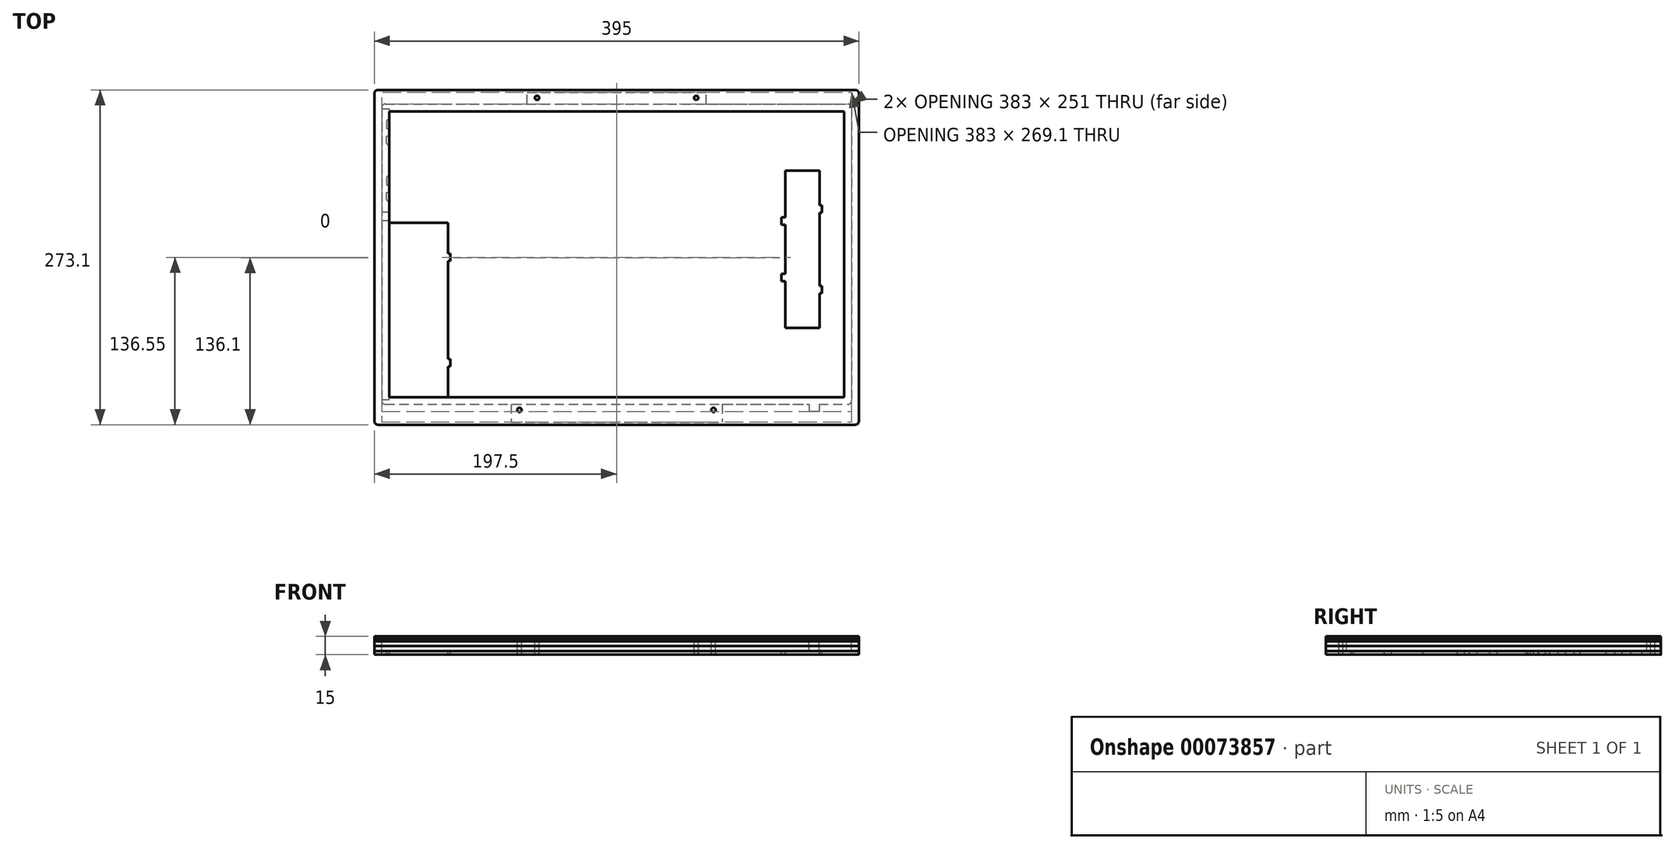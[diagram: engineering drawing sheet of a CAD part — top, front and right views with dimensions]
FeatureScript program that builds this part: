
annotation { "Feature Type Name" : "Feature", "Feature Type Description" : "" }
export const myFeature = defineFeature(function(context is Context, id is Id, definition is map)
    precondition{}
    {
        {
            var Q0;
            Q0=qCreatedBy(makeId("Top.planeOp"),FACE);
            var sketch = newSketch(context, id + "F0", { "sketchPlane" : qUnion([Q0])});
            skLineSegment(sketch, "E0.bottom", {"start": v(3, 245) * mm, "end": v(380, 245) * mm});
            skLineSegment(sketch, "E0.top", {"start": v(3, 0) * mm, "end": v(107.5, 0) * mm});
            skLineSegment(sketch, "E0.left", {"start": v(0, 242) * mm, "end": v(0, 3) * mm});
            skLineSegment(sketch, "E0.right", {"start": v(383, 242) * mm, "end": v(383, 3) * mm});
            skLineSegment(sketch, "E1.bottom", {"start": v(7, 239) * mm, "end": v(376, 239) * mm});
            skLineSegment(sketch, "E1.top", {"start": v(7, 6) * mm, "end": v(376, 6) * mm});
            skLineSegment(sketch, "E1.left", {"start": v(6, 238) * mm, "end": v(6, 7) * mm});
            skLineSegment(sketch, "E1.right", {"start": v(377, 238) * mm, "end": v(377, 7) * mm});
            skLineSegment(sketch, "E2.bottom", {"start": v(124, 253.5) * mm, "end": v(139, 253.5) * mm});
            skLineSegment(sketch, "E2.top", {"start": v(120.5, 245) * mm, "end": v(142.5, 245) * mm});
            skLineSegment(sketch, "E2.left", {"start": v(120.5, 250) * mm, "end": v(120.5, 245) * mm});
            skLineSegment(sketch, "E2.right", {"start": v(142.5, 250) * mm, "end": v(142.5, 245) * mm});
            skPoint(sketch, "E3.visualSharp", {"position": v(6, 239) * mm});
            skArc(sketch, "E3.filletArc", {"start": v(7, 239) * mm, "mid": v(6.3, 238.7) * mm, "end": v(6, 238) * mm});
            skPoint(sketch, "E4.visualSharp", {"position": v(377, 239) * mm});
            skArc(sketch, "E4.filletArc", {"start": v(377, 238) * mm, "mid": v(376.7, 238.7) * mm, "end": v(376, 239) * mm});
            skPoint(sketch, "E5.visualSharp", {"position": v(377, 6) * mm});
            skArc(sketch, "E5.filletArc", {"start": v(376, 6) * mm, "mid": v(376.7, 6.3) * mm, "end": v(377, 7) * mm});
            skPoint(sketch, "E6.visualSharp", {"position": v(6, 6) * mm});
            skArc(sketch, "E6.filletArc", {"start": v(6, 7) * mm, "mid": v(6.3, 6.3) * mm, "end": v(7, 6) * mm});
            skPoint(sketch, "E7.visualSharp", {"position": v(0, 245) * mm});
            skArc(sketch, "E7.filletArc", {"start": v(3, 245) * mm, "mid": v(0.88, 244.12) * mm, "end": v(0, 242) * mm});
            skPoint(sketch, "E8.visualSharp", {"position": v(383, 245) * mm});
            skArc(sketch, "E8.filletArc", {"start": v(383, 242) * mm, "mid": v(382.12, 244.12) * mm, "end": v(380, 245) * mm});
            skPoint(sketch, "E9.visualSharp", {"position": v(383, 0) * mm});
            skArc(sketch, "E9.filletArc", {"start": v(380, 0) * mm, "mid": v(382.12, 0.88) * mm, "end": v(383, 3) * mm});
            skPoint(sketch, "E10.visualSharp", {"position": v(0, 0) * mm});
            skArc(sketch, "E10.filletArc", {"start": v(0, 3) * mm, "mid": v(0.88, 0.88) * mm, "end": v(3, 0) * mm});
            skLineSegment(sketch, "E11", {"start": v(191.5, 299.4) * mm, "end": v(191.5, -28.7) * mm, "construction": true});
            skPoint(sketch, "E11.startSnap0", {"position": v(191.5, 245) * mm});
            skPoint(sketch, "E12.visualSharp", {"position": v(120.5, 253.5) * mm});
            skArc(sketch, "E12.filletArc", {"start": v(124, 253.5) * mm, "mid": v(121.53, 252.47) * mm, "end": v(120.5, 250) * mm});
            skPoint(sketch, "E13.visualSharp", {"position": v(142.5, 253.5) * mm});
            skArc(sketch, "E13.filletArc", {"start": v(142.5, 250) * mm, "mid": v(141.47, 252.47) * mm, "end": v(139, 253.5) * mm});
            skLineSegment(sketch, "E14.bottom", {"start": v(124.4, 251.75) * mm, "end": v(128.9, 251.75) * mm});
            skLineSegment(sketch, "E14.top", {"start": v(124.4, 248.25) * mm, "end": v(128.9, 248.25) * mm});
            skArc(sketch, "E15", {"start": v(128.9, 251.75) * mm, "mid": v(129.5, 250) * mm, "end": v(128.9, 248.25) * mm});
            skPoint(sketch, "E15.centerSnap0", {"position": v(126.65, 251.75) * mm});
            skPoint(sketch, "E15.centerSnap1", {"position": v(124.4, 250) * mm});
            skArc(sketch, "E16", {"start": v(124.4, 251.75) * mm, "mid": v(123.8, 250) * mm, "end": v(124.4, 248.25) * mm});
            skCircle(sketch, "E17", {"center": v(137.35, 250) * mm, "radius": 1.75 * mm});
            skArc(sketch, "E18.MirrorCS", {"start": v(258.6, 251.75) * mm, "mid": v(259.2, 250) * mm, "end": v(258.6, 248.25) * mm});
            skLineSegment(sketch, "E19.MirrorCS", {"start": v(258.6, 251.75) * mm, "end": v(254.1, 251.75) * mm});
            skArc(sketch, "E20.MirrorCS", {"start": v(254.1, 251.75) * mm, "mid": v(253.5, 250) * mm, "end": v(254.1, 248.25) * mm});
            skLineSegment(sketch, "E21.MirrorCS", {"start": v(240.5, 250) * mm, "end": v(240.5, 245) * mm});
            skLineSegment(sketch, "E22.MirrorCS", {"start": v(262.5, 250) * mm, "end": v(262.5, 245) * mm});
            skLineSegment(sketch, "E23.MirrorCS", {"start": v(259, 253.5) * mm, "end": v(244, 253.5) * mm});
            skPoint(sketch, "E24.MirrorP", {"position": v(256.35, 251.75) * mm});
            skArc(sketch, "E25.MirrorCS", {"start": v(240.5, 250) * mm, "mid": v(241.53, 252.47) * mm, "end": v(244, 253.5) * mm});
            skLineSegment(sketch, "E26.MirrorCS", {"start": v(258.6, 248.25) * mm, "end": v(254.1, 248.25) * mm});
            skArc(sketch, "E27.MirrorCS", {"start": v(259, 253.5) * mm, "mid": v(261.47, 252.47) * mm, "end": v(262.5, 250) * mm});
            skPoint(sketch, "E28.MirrorP", {"position": v(258.6, 250) * mm});
            skPoint(sketch, "E29.MirrorP", {"position": v(262.5, 253.5) * mm});
            skLineSegment(sketch, "E30.MirrorCS", {"start": v(262.5, 245) * mm, "end": v(240.5, 245) * mm});
            skPoint(sketch, "E31.MirrorP", {"position": v(240.5, 253.5) * mm});
            skCircle(sketch, "E32.MirrorC", {"center": v(245.65, 250) * mm, "radius": 1.75 * mm});
            skLineSegment(sketch, "E33.bottom", {"start": v(265.5, 0) * mm, "end": v(275.5, 0) * mm});
            skLineSegment(sketch, "E33.top", {"start": v(269, -9) * mm, "end": v(272, -9) * mm});
            skLineSegment(sketch, "E33.left", {"start": v(265.5, 0) * mm, "end": v(265.5, -5.5) * mm});
            skLineSegment(sketch, "E33.right", {"start": v(275.5, 0) * mm, "end": v(275.5, -5.5) * mm});
            skPoint(sketch, "E34.visualSharp", {"position": v(265.5, -9) * mm});
            skArc(sketch, "E34.filletArc", {"start": v(265.5, -5.5) * mm, "mid": v(266.53, -7.97) * mm, "end": v(269, -9) * mm});
            skPoint(sketch, "E35.visualSharp", {"position": v(275.5, -9) * mm});
            skArc(sketch, "E35.filletArc", {"start": v(272, -9) * mm, "mid": v(274.47, -7.97) * mm, "end": v(275.5, -5.5) * mm});
            skCircle(sketch, "E36", {"center": v(270.5, -4.5) * mm, "radius": 1.75 * mm});
            skPoint(sketch, "E36.centerSnap0", {"position": v(270.5, -9) * mm});
            skLineSegment(sketch, "E37.bottom", {"start": v(107.5, 0) * mm, "end": v(116, 0) * mm});
            skLineSegment(sketch, "E37.top", {"start": v(111, -9) * mm, "end": v(116.5, -9) * mm});
            skLineSegment(sketch, "E37.left", {"start": v(107.5, 0) * mm, "end": v(107.5, -5.5) * mm});
            skPoint(sketch, "E38.visualSharp", {"position": v(107.5, -9) * mm});
            skArc(sketch, "E38.filletArc", {"start": v(107.5, -5.5) * mm, "mid": v(108.53, -7.97) * mm, "end": v(111, -9) * mm});
            skCircle(sketch, "E39", {"center": v(112.25, -4.5) * mm, "radius": 1.75 * mm});
            skLineSegment(sketch, "E40", {"start": v(116.5, -9) * mm, "end": v(116.5, -13) * mm});
            skLineSegment(sketch, "E41", {"start": v(116.5, -13) * mm, "end": v(119.9, -13) * mm});
            skLineSegment(sketch, "E42", {"start": v(119.9, -13) * mm, "end": v(119.9, -5.9) * mm});
            skLineSegment(sketch, "E43", {"start": v(120.4, -5.4) * mm, "end": v(122.4, -5.4) * mm});
            skLineSegment(sketch, "E44", {"start": v(122.4, -5.4) * mm, "end": v(122.4, 0) * mm});
            skLineSegment(sketch, "E45.trimOffspring", {"start": v(116.5, 0) * mm, "end": v(380, 0) * mm});
            skPoint(sketch, "E46.visualSharp", {"position": v(119.9, -5.4) * mm});
            skArc(sketch, "E46.filletArc", {"start": v(120.4, -5.4) * mm, "mid": v(120.05, -5.55) * mm, "end": v(119.9, -5.9) * mm});
            skLineSegment(sketch, "E47.0", {"start": v(125, -8) * mm, "end": v(125, 0) * mm});
            skLineSegment(sketch, "E47.1", {"start": v(122.5, -8) * mm, "end": v(125, -8) * mm});
            skLineSegment(sketch, "E47.2", {"start": v(122.5, -13.6) * mm, "end": v(122.5, -8) * mm});
            skLineSegment(sketch, "E48", {"start": v(122.5, -13.6) * mm, "end": v(135.6, -13.6) * mm});
            skLineSegment(sketch, "E49", {"start": v(252.5, -13.6) * mm, "end": v(252.5, 0) * mm});
            skCircle(sketch, "E50", {"center": v(125.35, -10.65) * mm, "radius": 1.75 * mm});
            skLineSegment(sketch, "E51", {"start": v(135.6, -13.6) * mm, "end": v(135.6, -11.3) * mm});
            skLineSegment(sketch, "E52", {"start": v(136.6, -10.3) * mm, "end": v(180.6, -10.3) * mm});
            skLineSegment(sketch, "E53", {"start": v(181.6, -11.3) * mm, "end": v(181.6, -13.6) * mm});
            skLineSegment(sketch, "E54.trimOffspring", {"start": v(181.6, -13.6) * mm, "end": v(252.5, -13.6) * mm});
            skPoint(sketch, "E55.visualSharp", {"position": v(135.6, -10.3) * mm});
            skArc(sketch, "E55.filletArc", {"start": v(136.6, -10.3) * mm, "mid": v(135.9, -10.6) * mm, "end": v(135.6, -11.3) * mm});
            skPoint(sketch, "E56.visualSharp", {"position": v(181.6, -10.3) * mm});
            skArc(sketch, "E56.filletArc", {"start": v(181.6, -11.3) * mm, "mid": v(181.3, -10.6) * mm, "end": v(180.6, -10.3) * mm});
            skLineSegment(sketch, "E57.bottom", {"start": v(356.5, 0) * mm, "end": v(348.5, 0) * mm});
            skLineSegment(sketch, "E57.top", {"start": v(356.5, -6) * mm, "end": v(348.5, -6) * mm});
            skLineSegment(sketch, "E57.left", {"start": v(356.5, 0) * mm, "end": v(356.5, -6) * mm});
            skLineSegment(sketch, "E57.right", {"start": v(348.5, 0) * mm, "end": v(348.5, -6) * mm});
            skSolve(sketch);
        }
        {
            var Q0;
            Q0=makeQuery(id+"F0.imprint","IMPRINT",FACE,{"disambiguationData":[TD([[makeQuery(id+"F0.imprint","IMPRINT",EDGE,{"derivedFrom":sQuery(id+"F0.wireOp",EDGE,"E1.bottom")}),-1.0]])]});
            var sketch = newSketch(context, id + "F1", { "sketchPlane" : qUnion([Q0])});
            skLineSegment(sketch, "E58.bottom", {"start": v(-3, 256.5) * mm, "end": v(386, 256.5) * mm});
            skLineSegment(sketch, "E58.top", {"start": v(-3, -16.6) * mm, "end": v(386, -16.6) * mm});
            skLineSegment(sketch, "E58.left", {"start": v(-6, 253.5) * mm, "end": v(-6, -13.6) * mm});
            skLineSegment(sketch, "E58.right", {"start": v(389, 253.5) * mm, "end": v(389, -13.6) * mm});
            skLineSegment(sketch, "E59.0", {"start": v(6, 239) * mm, "end": v(6, 6) * mm});
            skLineSegment(sketch, "E59.1", {"start": v(6, 239) * mm, "end": v(377, 239) * mm});
            skLineSegment(sketch, "E59.2", {"start": v(377, 239) * mm, "end": v(377, 6) * mm});
            skLineSegment(sketch, "E59.3", {"start": v(6, 6) * mm, "end": v(377, 6) * mm});
            skPoint(sketch, "E60.visualSharp", {"position": v(-6, 256.5) * mm});
            skArc(sketch, "E60.filletArc", {"start": v(-3, 256.5) * mm, "mid": v(-5.12, 255.62) * mm, "end": v(-6, 253.5) * mm});
            skPoint(sketch, "E61.visualSharp", {"position": v(389, 256.5) * mm});
            skArc(sketch, "E61.filletArc", {"start": v(389, 253.5) * mm, "mid": v(388.12, 255.62) * mm, "end": v(386, 256.5) * mm});
            skPoint(sketch, "E62.visualSharp", {"position": v(389, -16.6) * mm});
            skArc(sketch, "E62.filletArc", {"start": v(386, -16.6) * mm, "mid": v(388.12, -15.72) * mm, "end": v(389, -13.6) * mm});
            skPoint(sketch, "E63.visualSharp", {"position": v(-6, -16.6) * mm});
            skArc(sketch, "E63.filletArc", {"start": v(-6, -13.6) * mm, "mid": v(-5.12, -15.72) * mm, "end": v(-3, -16.6) * mm});
            skCircle(sketch, "E64", {"center": v(126.65, 250) * mm, "radius": 1.75 * mm});
            skCircle(sketch, "E65.0", {"center": v(112.25, -4.5) * mm, "radius": 1.75 * mm});
            skCircle(sketch, "E66.0", {"center": v(270.5, -4.5) * mm, "radius": 1.75 * mm});
            skPoint(sketch, "E67.0", {"position": v(256.35, 250) * mm});
            skCircle(sketch, "E68", {"center": v(256.35, 250) * mm, "radius": 1.75 * mm});
            skSolve(sketch);
        }
        {
            var Q0;
            Q0 = qSketchRegion(id + "F1", true);
            extrude(context, id + "F2", {"entities" : qUnion([Q0]), "depth" : 2 * mm});
        }
        {
            var Q0;
            Q0=makeQuery(id+"F0.imprint","IMPRINT",FACE,{"disambiguationData":[TD([[makeQuery(id+"F0.imprint","IMPRINT",EDGE,{"derivedFrom":sQuery(id+"F0.wireOp",EDGE,"E1.bottom")}),-1.0]])]});
            var sketch = newSketch(context, id + "F3", { "sketchPlane" : qUnion([Q0])});
            skLineSegment(sketch, "E69.0", {"start": v(-3, 256.5) * mm, "end": v(386, 256.5) * mm});
            skArc(sketch, "E70.0", {"start": v(-3, 256.5) * mm, "mid": v(-5.12, 255.62) * mm, "end": v(-6, 253.5) * mm});
            skLineSegment(sketch, "E71.0", {"start": v(-6, 253.5) * mm, "end": v(-6, -13.6) * mm});
            skArc(sketch, "E72.0", {"start": v(389, 253.5) * mm, "mid": v(388.12, 255.62) * mm, "end": v(386, 256.5) * mm});
            skLineSegment(sketch, "E73.0", {"start": v(389, 253.5) * mm, "end": v(389, -13.6) * mm});
            skArc(sketch, "E74.0", {"start": v(386, -16.6) * mm, "mid": v(388.12, -15.72) * mm, "end": v(389, -13.6) * mm});
            skLineSegment(sketch, "E75.0", {"start": v(-3, -16.6) * mm, "end": v(386, -16.6) * mm});
            skArc(sketch, "E76.0", {"start": v(-6, -13.6) * mm, "mid": v(-5.12, -15.72) * mm, "end": v(-3, -16.6) * mm});
            skLineSegment(sketch, "E77.0", {"start": v(0, 242) * mm, "end": v(0, 3) * mm});
            skArc(sketch, "E78.0", {"start": v(0, 3) * mm, "mid": v(0.88, 0.88) * mm, "end": v(3, 0) * mm});
            skLineSegment(sketch, "E79.0", {"start": v(3, 0) * mm, "end": v(105.5, 0) * mm});
            skArc(sketch, "E80.0", {"start": v(3, 245) * mm, "mid": v(0.88, 244.12) * mm, "end": v(0, 242) * mm});
            skLineSegment(sketch, "E81.0", {"start": v(3, 245) * mm, "end": v(118.5, 245) * mm});
            skArc(sketch, "E82.0", {"start": v(383, 242) * mm, "mid": v(382.12, 244.12) * mm, "end": v(380, 245) * mm});
            skLineSegment(sketch, "E83.0", {"start": v(383, 242) * mm, "end": v(383, 3) * mm});
            skArc(sketch, "E84.0", {"start": v(380, 0) * mm, "mid": v(382.12, 0.88) * mm, "end": v(383, 3) * mm});
            skLineSegment(sketch, "E85.0", {"start": v(277.5, 0) * mm, "end": v(380, 0) * mm});
            skLineSegment(sketch, "E86.top", {"start": v(105.5, -14.6) * mm, "end": v(277.5, -14.6) * mm});
            skLineSegment(sketch, "E86.left", {"start": v(105.5, 0) * mm, "end": v(105.5, -14.6) * mm});
            skLineSegment(sketch, "E86.right", {"start": v(277.5, 0) * mm, "end": v(277.5, -14.6) * mm});
            skPoint(sketch, "E86.bottom.end.orphan", {"position": v(107.5, 0) * mm});
            skPoint(sketch, "E87.trimOffspring.start.orphan", {"position": v(116, 0) * mm});
            skPoint(sketch, "E88.orphan", {"position": v(116.5, 0) * mm});
            skLineSegment(sketch, "E89.top", {"start": v(118.5, 254.5) * mm, "end": v(264.5, 254.5) * mm});
            skLineSegment(sketch, "E89.left", {"start": v(118.5, 245) * mm, "end": v(118.5, 254.5) * mm});
            skLineSegment(sketch, "E89.right", {"start": v(264.5, 245) * mm, "end": v(264.5, 254.5) * mm});
            skLineSegment(sketch, "E90.trimOffspring", {"start": v(264.5, 245) * mm, "end": v(380, 245) * mm});
            skLineSegment(sketch, "E91.0", {"start": v(348.5, 0) * mm, "end": v(348.5, -6) * mm});
            skLineSegment(sketch, "E91.1", {"start": v(356.5, -6) * mm, "end": v(348.5, -6) * mm});
            skLineSegment(sketch, "E91.2", {"start": v(356.5, 0) * mm, "end": v(356.5, -6) * mm});
            skSolve(sketch);
        }
        {
            var Q0;
            Q0 = qSketchRegion(id + "F3", true);
            extrude(context, id + "F4", {"entities" : qUnion([Q0]), "oppositeDirection" : true, "depth" : 2 * mm});
        }
        {
            var Q0;
            Q0=makeQuery(id+"F3.imprint","IMPRINT",FACE,{"disambiguationData":[TD([[makeQuery(id+"F3.imprint","IMPRINT",EDGE,{"derivedFrom":makeQuery(id+"F0.imprint","IMPRINT",EDGE,{"derivedFrom":sQuery(id+"F0.wireOp",EDGE,"E1.bottom")})}),-1.0]])]});
            var sketch = newSketch(context, id + "F5", { "sketchPlane" : qUnion([Q0])});
            skLineSegment(sketch, "E92.0", {"start": v(-3, 256.5) * mm, "end": v(386, 256.5) * mm});
            skArc(sketch, "E92.1", {"start": v(-3, 256.5) * mm, "mid": v(-5.12, 255.62) * mm, "end": v(-6, 253.5) * mm});
            skLineSegment(sketch, "E92.2", {"start": v(-6, 253.5) * mm, "end": v(-6, -13.6) * mm});
            skArc(sketch, "E92.3", {"start": v(-6, -13.6) * mm, "mid": v(-5.12, -15.72) * mm, "end": v(-3, -16.6) * mm});
            skLineSegment(sketch, "E92.4", {"start": v(-3, -16.6) * mm, "end": v(386, -16.6) * mm});
            skArc(sketch, "E92.5", {"start": v(386, -16.6) * mm, "mid": v(388.12, -15.72) * mm, "end": v(389, -13.6) * mm});
            skLineSegment(sketch, "E92.6", {"start": v(389, 253.5) * mm, "end": v(389, -13.6) * mm});
            skArc(sketch, "E92.7", {"start": v(389, 253.5) * mm, "mid": v(388.12, 255.62) * mm, "end": v(386, 256.5) * mm});
            skLineSegment(sketch, "E92.8", {"start": v(264.5, 245) * mm, "end": v(380, 245) * mm});
            skArc(sketch, "E92.9", {"start": v(383, 242) * mm, "mid": v(382.12, 244.12) * mm, "end": v(380, 245) * mm});
            skLineSegment(sketch, "E92.10", {"start": v(383, 242) * mm, "end": v(383, 3) * mm});
            skArc(sketch, "E92.11", {"start": v(380, 0) * mm, "mid": v(382.12, 0.88) * mm, "end": v(383, 3) * mm});
            skLineSegment(sketch, "E92.12", {"start": v(277.5, 0) * mm, "end": v(348.5, 0) * mm});
            skLineSegment(sketch, "E92.13", {"start": v(356.5, 0) * mm, "end": v(356.5, -6) * mm});
            skLineSegment(sketch, "E92.14", {"start": v(356.5, -6) * mm, "end": v(348.5, -6) * mm});
            skLineSegment(sketch, "E92.15", {"start": v(348.5, 0) * mm, "end": v(348.5, -6) * mm});
            skLineSegment(sketch, "E92.16", {"start": v(3, 0) * mm, "end": v(105.5, 0) * mm});
            skArc(sketch, "E92.17", {"start": v(0, 3) * mm, "mid": v(0.88, 0.88) * mm, "end": v(3, 0) * mm});
            skLineSegment(sketch, "E92.18", {"start": v(0, 242) * mm, "end": v(0, 3) * mm});
            skArc(sketch, "E92.19", {"start": v(3, 245) * mm, "mid": v(0.88, 244.12) * mm, "end": v(0, 242) * mm});
            skLineSegment(sketch, "E92.20", {"start": v(3, 245) * mm, "end": v(118.5, 245) * mm});
            skLineSegment(sketch, "E93", {"start": v(118.5, 245) * mm, "end": v(264.5, 245) * mm});
            skLineSegment(sketch, "E94", {"start": v(105.5, 0) * mm, "end": v(277.5, 0) * mm});
            skCircle(sketch, "E95.0", {"center": v(126.65, 250) * mm, "radius": 1.75 * mm});
            skCircle(sketch, "E95.2", {"center": v(270.5, -4.5) * mm, "radius": 1.75 * mm});
            skCircle(sketch, "E95.3", {"center": v(112.25, -4.5) * mm, "radius": 1.75 * mm});
            skCircle(sketch, "E96.0", {"center": v(256.35, 250) * mm, "radius": 1.75 * mm});
            skLineSegment(sketch, "E97", {"start": v(356.5, 0) * mm, "end": v(380, 0) * mm});
            skSolve(sketch);
        }
        {
            var Q0;
            Q0 = qSketchRegion(id + "F5", true);
            extrude(context, id + "F6", {"entities" : qUnion([Q0]), "oppositeDirection" : true, "depth" : 4 * mm});
        }
        {
            var Q0;
            Q0=makeQuery(id+"F6.opExtrude","SWEPT_BODY",BODY,{"disambiguationData":[OSD([sQuery(id+"F5.wireOp",EDGE,"E92.0"),sQuery(id+"F5.wireOp",EDGE,"E92.1"),sQuery(id+"F5.wireOp",EDGE,"E92.2"),sQuery(id+"F5.wireOp",EDGE,"E92.3"),sQuery(id+"F5.wireOp",EDGE,"E92.4"),sQuery(id+"F5.wireOp",EDGE,"E92.5"),sQuery(id+"F5.wireOp",EDGE,"E92.6"),sQuery(id+"F5.wireOp",EDGE,"E92.7"),sQuery(id+"F5.wireOp",EDGE,"E92.8"),sQuery(id+"F5.wireOp",EDGE,"E92.9"),sQuery(id+"F5.wireOp",EDGE,"E92.10"),sQuery(id+"F5.wireOp",EDGE,"E92.11"),sQuery(id+"F5.wireOp",EDGE,"E92.12"),sQuery(id+"F5.wireOp",EDGE,"E92.13"),sQuery(id+"F5.wireOp",EDGE,"E92.14"),sQuery(id+"F5.wireOp",EDGE,"E92.15"),sQuery(id+"F5.wireOp",EDGE,"E92.16"),sQuery(id+"F5.wireOp",EDGE,"E92.17"),sQuery(id+"F5.wireOp",EDGE,"E92.18"),sQuery(id+"F5.wireOp",EDGE,"E92.19"),sQuery(id+"F5.wireOp",EDGE,"E92.20"),sQuery(id+"F5.wireOp",EDGE,"E93"),sQuery(id+"F5.wireOp",EDGE,"E94"),sQuery(id+"F5.wireOp",EDGE,"E95.0"),sQuery(id+"F5.wireOp",EDGE,"E95.1"),sQuery(id+"F5.wireOp",EDGE,"E95.2"),sQuery(id+"F5.wireOp",EDGE,"E95.3")])]});
            transform(context, id + "F7", {"entities" : qUnion([Q0]), "transformType" : TransformType.TRANSLATION_3D, "dx" : 0 * mm, "dy" : 0 * mm, "dz" : -2 * mm, "makeCopy" : false});
        }
        {
            var Q0;
            Q0=makeQuery(id+"F6.opExtrude","SWEPT_BODY",BODY,{"disambiguationData":[OSD([sQuery(id+"F5.wireOp",EDGE,"E92.0"),sQuery(id+"F5.wireOp",EDGE,"E92.1"),sQuery(id+"F5.wireOp",EDGE,"E92.2"),sQuery(id+"F5.wireOp",EDGE,"E92.3"),sQuery(id+"F5.wireOp",EDGE,"E92.4"),sQuery(id+"F5.wireOp",EDGE,"E92.5"),sQuery(id+"F5.wireOp",EDGE,"E92.6"),sQuery(id+"F5.wireOp",EDGE,"E92.7"),sQuery(id+"F5.wireOp",EDGE,"E92.8"),sQuery(id+"F5.wireOp",EDGE,"E92.9"),sQuery(id+"F5.wireOp",EDGE,"E92.10"),sQuery(id+"F5.wireOp",EDGE,"E92.11"),sQuery(id+"F5.wireOp",EDGE,"E92.12"),sQuery(id+"F5.wireOp",EDGE,"E92.13"),sQuery(id+"F5.wireOp",EDGE,"E92.14"),sQuery(id+"F5.wireOp",EDGE,"E92.15"),sQuery(id+"F5.wireOp",EDGE,"E92.16"),sQuery(id+"F5.wireOp",EDGE,"E92.17"),sQuery(id+"F5.wireOp",EDGE,"E92.18"),sQuery(id+"F5.wireOp",EDGE,"E92.19"),sQuery(id+"F5.wireOp",EDGE,"E92.20"),sQuery(id+"F5.wireOp",EDGE,"E93"),sQuery(id+"F5.wireOp",EDGE,"E94"),sQuery(id+"F5.wireOp",EDGE,"E95.0"),sQuery(id+"F5.wireOp",EDGE,"E95.1"),sQuery(id+"F5.wireOp",EDGE,"E95.2"),sQuery(id+"F5.wireOp",EDGE,"E95.3")])]});
            transform(context, id + "F8", {"entities" : qUnion([Q0]), "transformType" : TransformType.TRANSLATION_3D, "dx" : 0 * mm, "dy" : 0 * mm, "dz" : -4 * mm, "makeCopy" : true});
        }
        {
            var Q0;
            Q0=makeQuery(id+"F8.opPattern","COPY",FACE,{"derivedFrom":makeQuery(id+"F6.opExtrude","CAP_FACE",FACE,{"disambiguationData":[OSD([sQuery(id+"F5.wireOp",EDGE,"E92.0"),sQuery(id+"F5.wireOp",EDGE,"E92.1"),sQuery(id+"F5.wireOp",EDGE,"E92.2"),sQuery(id+"F5.wireOp",EDGE,"E92.3"),sQuery(id+"F5.wireOp",EDGE,"E92.4"),sQuery(id+"F5.wireOp",EDGE,"E92.5"),sQuery(id+"F5.wireOp",EDGE,"E92.6"),sQuery(id+"F5.wireOp",EDGE,"E92.7"),sQuery(id+"F5.wireOp",EDGE,"E92.8"),sQuery(id+"F5.wireOp",EDGE,"E92.9"),sQuery(id+"F5.wireOp",EDGE,"E92.10"),sQuery(id+"F5.wireOp",EDGE,"E92.11"),sQuery(id+"F5.wireOp",EDGE,"E92.12"),sQuery(id+"F5.wireOp",EDGE,"E92.13"),sQuery(id+"F5.wireOp",EDGE,"E92.14"),sQuery(id+"F5.wireOp",EDGE,"E92.15"),sQuery(id+"F5.wireOp",EDGE,"E92.16"),sQuery(id+"F5.wireOp",EDGE,"E92.17"),sQuery(id+"F5.wireOp",EDGE,"E92.18"),sQuery(id+"F5.wireOp",EDGE,"E92.19"),sQuery(id+"F5.wireOp",EDGE,"E92.20"),sQuery(id+"F5.wireOp",EDGE,"E93"),sQuery(id+"F5.wireOp",EDGE,"E94"),sQuery(id+"F5.wireOp",EDGE,"E95.0"),sQuery(id+"F5.wireOp",EDGE,"E95.1"),sQuery(id+"F5.wireOp",EDGE,"E95.2"),sQuery(id+"F5.wireOp",EDGE,"E95.3")])],"isStart":false}),"instanceName":"1"});
            var sketch = newSketch(context, id + "F9", { "sketchPlane" : qUnion([Q0])});
            skLineSegment(sketch, "E98.0", {"start": v(-6, -253.5) * mm, "end": v(-6, 13.6) * mm});
            skArc(sketch, "E98.1", {"start": v(-3, -256.5) * mm, "mid": v(-5.12, -255.62) * mm, "end": v(-6, -253.5) * mm});
            skLineSegment(sketch, "E98.2", {"start": v(-3, -256.5) * mm, "end": v(386, -256.5) * mm});
            skArc(sketch, "E98.3", {"start": v(389, -253.5) * mm, "mid": v(388.12, -255.62) * mm, "end": v(386, -256.5) * mm});
            skLineSegment(sketch, "E98.4", {"start": v(389, -253.5) * mm, "end": v(389, 13.6) * mm});
            skArc(sketch, "E98.5", {"start": v(386, 16.6) * mm, "mid": v(388.12, 15.72) * mm, "end": v(389, 13.6) * mm});
            skLineSegment(sketch, "E98.6", {"start": v(-3, 16.6) * mm, "end": v(386, 16.6) * mm});
            skArc(sketch, "E98.7", {"start": v(-6, 13.6) * mm, "mid": v(-5.12, 15.72) * mm, "end": v(-3, 16.6) * mm});
            skCircle(sketch, "E99.0", {"center": v(112.25, 4.5) * mm, "radius": 1.75 * mm});
            skCircle(sketch, "E99.1", {"center": v(270.5, 4.5) * mm, "radius": 1.75 * mm});
            skCircle(sketch, "E99.2", {"center": v(126.65, -250) * mm, "radius": 1.75 * mm});
            skLineSegment(sketch, "E100.bottom", {"start": v(357, -162.5) * mm, "end": v(359, -162.5) * mm});
            skLineSegment(sketch, "E100.top", {"start": v(357, -156.5) * mm, "end": v(359, -156.5) * mm});
            skLineSegment(sketch, "E100.right", {"start": v(359, -162.5) * mm, "end": v(359, -156.5) * mm});
            skLineSegment(sketch, "E101", {"start": v(407.88, -126.5) * mm, "end": v(-12.86, -126.5) * mm, "construction": true});
            skLineSegment(sketch, "E102.MirrorCS", {"start": v(357, -96.5) * mm, "end": v(359, -96.5) * mm});
            skLineSegment(sketch, "E103.MirrorCS", {"start": v(359, -90.5) * mm, "end": v(359, -96.5) * mm});
            skLineSegment(sketch, "E104.MirrorCS", {"start": v(357, -90.5) * mm, "end": v(359, -90.5) * mm});
            skLineSegment(sketch, "E105.rect.bottom", {"start": v(357, -190.5) * mm, "end": v(329, -190.5) * mm});
            skLineSegment(sketch, "E105.rect.top", {"start": v(357, -62.5) * mm, "end": v(329, -62.5) * mm});
            skLineSegment(sketch, "E105.rect.left", {"start": v(357, -190.5) * mm, "end": v(357, -162.5) * mm});
            skLineSegment(sketch, "E105.rect.right", {"start": v(329, -190.5) * mm, "end": v(329, -152.5) * mm});
            skPoint(sketch, "E105.rect.middle", {"position": v(343, -126.5) * mm});
            skLineSegment(sketch, "E106.trimOffspring", {"start": v(357, -156.5) * mm, "end": v(357, -96.5) * mm});
            skPoint(sketch, "E107.MirrorCS.end.orphan", {"position": v(357, -96.5) * mm});
            skPoint(sketch, "E107.MirrorCS.start.orphan", {"position": v(357, -90.5) * mm});
            skLineSegment(sketch, "E108.trimOffspring", {"start": v(357, -90.5) * mm, "end": v(357, -62.5) * mm});
            skLineSegment(sketch, "E109", {"start": v(329, -152.5) * mm, "end": v(326, -152.5) * mm});
            skLineSegment(sketch, "E110", {"start": v(326, -152.5) * mm, "end": v(326, -146.5) * mm});
            skLineSegment(sketch, "E111", {"start": v(326, -146.5) * mm, "end": v(329, -146.5) * mm});
            skLineSegment(sketch, "E112.trimOffspring", {"start": v(329, -146.5) * mm, "end": v(329, -106.5) * mm});
            skLineSegment(sketch, "E113.MirrorCS", {"start": v(329, -100.5) * mm, "end": v(326, -100.5) * mm});
            skLineSegment(sketch, "E114.MirrorCS", {"start": v(326, -100.5) * mm, "end": v(326, -106.5) * mm});
            skLineSegment(sketch, "E115.MirrorCS", {"start": v(326, -106.5) * mm, "end": v(329, -106.5) * mm});
            skLineSegment(sketch, "E116.trimOffspring", {"start": v(329, -100.5) * mm, "end": v(329, -62.5) * mm});
            skLineSegment(sketch, "E117.bottom", {"start": v(0, -148) * mm, "end": v(0, -148) * mm});
            skLineSegment(sketch, "E117.top", {"start": v(0, -6) * mm, "end": v(0, -6) * mm});
            skLineSegment(sketch, "E117.left", {"start": v(0, -148) * mm, "end": v(0, -6) * mm});
            skLineSegment(sketch, "E117.right", {"start": v(54, -148) * mm, "end": v(54, -123) * mm});
            skLineSegment(sketch, "E118", {"start": v(54, -37) * mm, "end": v(56, -37) * mm});
            skLineSegment(sketch, "E119", {"start": v(56, -37) * mm, "end": v(56, -31) * mm});
            skLineSegment(sketch, "E120", {"start": v(56, -31) * mm, "end": v(54, -31) * mm});
            skLineSegment(sketch, "E121.trimOffspring", {"start": v(54, -31) * mm, "end": v(54, -6) * mm});
            skLineSegment(sketch, "E122", {"start": v(-8.9, -77) * mm, "end": v(64.44, -77) * mm, "construction": true});
            skPoint(sketch, "E122.startSnap0", {"position": v(0, -77) * mm});
            skLineSegment(sketch, "E123.MirrorCS", {"start": v(56, -123) * mm, "end": v(54, -123) * mm});
            skLineSegment(sketch, "E124.MirrorCS", {"start": v(56, -117) * mm, "end": v(56, -123) * mm});
            skLineSegment(sketch, "E125.MirrorCS", {"start": v(54, -117) * mm, "end": v(56, -117) * mm});
            skLineSegment(sketch, "E126.trimOffspring", {"start": v(54, -117) * mm, "end": v(54, -37) * mm});
            skLineSegment(sketch, "E127", {"start": v(0, -6) * mm, "end": v(0, -4) * mm});
            skLineSegment(sketch, "E128", {"start": v(0, -4) * mm, "end": v(6, -4) * mm});
            skLineSegment(sketch, "E129", {"start": v(6, -4) * mm, "end": v(6, -6) * mm});
            skLineSegment(sketch, "E130.trimOffspring", {"start": v(6, -6) * mm, "end": v(54, -6) * mm});
            skLineSegment(sketch, "E131.MirrorCS", {"start": v(0, -148) * mm, "end": v(0, -150) * mm});
            skLineSegment(sketch, "E132.MirrorCS", {"start": v(0, -150) * mm, "end": v(6, -150) * mm});
            skLineSegment(sketch, "E133.MirrorCS", {"start": v(6, -150) * mm, "end": v(6, -148) * mm});
            skLineSegment(sketch, "E134.trimOffspring", {"start": v(6, -148) * mm, "end": v(54, -148) * mm});
            skCircle(sketch, "E135.0", {"center": v(256.35, -250) * mm, "radius": 1.75 * mm});
            skLineSegment(sketch, "E136.bottom", {"start": v(0, -241) * mm, "end": v(6, -241) * mm});
            skLineSegment(sketch, "E136.top", {"start": v(0, -157) * mm, "end": v(6, -157) * mm});
            skLineSegment(sketch, "E136.left", {"start": v(0, -241) * mm, "end": v(0, -157) * mm});
            skLineSegment(sketch, "E136.right", {"start": v(6, -241) * mm, "end": v(6, -233) * mm});
            skLineSegment(sketch, "E137", {"start": v(-19.04, -199) * mm, "end": v(16.77, -199) * mm, "construction": true});
            skPoint(sketch, "E137.startSnap0", {"position": v(0, -199) * mm});
            skLineSegment(sketch, "E138", {"start": v(-14.9, -176) * mm, "end": v(21.76, -176) * mm, "construction": true});
            skLineSegment(sketch, "E139", {"start": v(5, -186) * mm, "end": v(5, -186) * mm});
            skLineSegment(sketch, "E140", {"start": v(4, -185) * mm, "end": v(4, -179) * mm});
            skLineSegment(sketch, "E141", {"start": v(4, -179) * mm, "end": v(6, -179) * mm});
            skLineSegment(sketch, "E142.trimOffspring", {"start": v(6, -179) * mm, "end": v(6, -173) * mm});
            skLineSegment(sketch, "E143.MirrorCS", {"start": v(5, -166) * mm, "end": v(5, -166) * mm});
            skLineSegment(sketch, "E144.MirrorCS", {"start": v(4, -167) * mm, "end": v(4, -173) * mm});
            skLineSegment(sketch, "E145.MirrorCS", {"start": v(4, -173) * mm, "end": v(6, -173) * mm});
            skLineSegment(sketch, "E146.trimOffspring", {"start": v(6, -165) * mm, "end": v(6, -157) * mm});
            skPoint(sketch, "E147.visualSharp", {"position": v(4, -186) * mm});
            skArc(sketch, "E147.filletArc", {"start": v(4, -185) * mm, "mid": v(4.3, -185.7) * mm, "end": v(5, -186) * mm});
            skPoint(sketch, "E148.visualSharp", {"position": v(6, -186) * mm});
            skArc(sketch, "E148.filletArc", {"start": v(6, -187) * mm, "mid": v(5.7, -186.3) * mm, "end": v(5, -186) * mm});
            skPoint(sketch, "E149.visualSharp", {"position": v(4, -166) * mm});
            skArc(sketch, "E149.filletArc", {"start": v(5, -166) * mm, "mid": v(4.3, -166.3) * mm, "end": v(4, -167) * mm});
            skPoint(sketch, "E150.visualSharp", {"position": v(6, -166) * mm});
            skArc(sketch, "E150.filletArc", {"start": v(5, -166) * mm, "mid": v(5.7, -165.7) * mm, "end": v(6, -165) * mm});
            skArc(sketch, "E151.MirrorCS", {"start": v(6, -211) * mm, "mid": v(5.7, -211.7) * mm, "end": v(5, -212) * mm});
            skArc(sketch, "E152.MirrorCS", {"start": v(4, -213) * mm, "mid": v(4.3, -212.3) * mm, "end": v(5, -212) * mm});
            skLineSegment(sketch, "E153.MirrorCS", {"start": v(4, -213) * mm, "end": v(4, -219) * mm});
            skLineSegment(sketch, "E154.MirrorCS", {"start": v(4, -219) * mm, "end": v(6, -219) * mm});
            skLineSegment(sketch, "E155.MirrorCS", {"start": v(4, -225) * mm, "end": v(6, -225) * mm});
            skLineSegment(sketch, "E156.MirrorCS", {"start": v(4, -231) * mm, "end": v(4, -225) * mm});
            skArc(sketch, "E157.MirrorCS", {"start": v(5, -232) * mm, "mid": v(4.3, -231.7) * mm, "end": v(4, -231) * mm});
            skArc(sketch, "E158.MirrorCS", {"start": v(5, -232) * mm, "mid": v(5.7, -232.3) * mm, "end": v(6, -233) * mm});
            skLineSegment(sketch, "E159.trimOffspring", {"start": v(6, -225) * mm, "end": v(6, -219) * mm});
            skLineSegment(sketch, "E160.trimOffspring", {"start": v(6, -211) * mm, "end": v(6, -187) * mm});
            skSolve(sketch);
        }
        {
            var Q0;
            Q0 = qSketchRegion(id + "F9", true);
            extrude(context, id + "F10", {"entities" : qUnion([Q0]), "depth" : 3 * mm});
        }
    });
